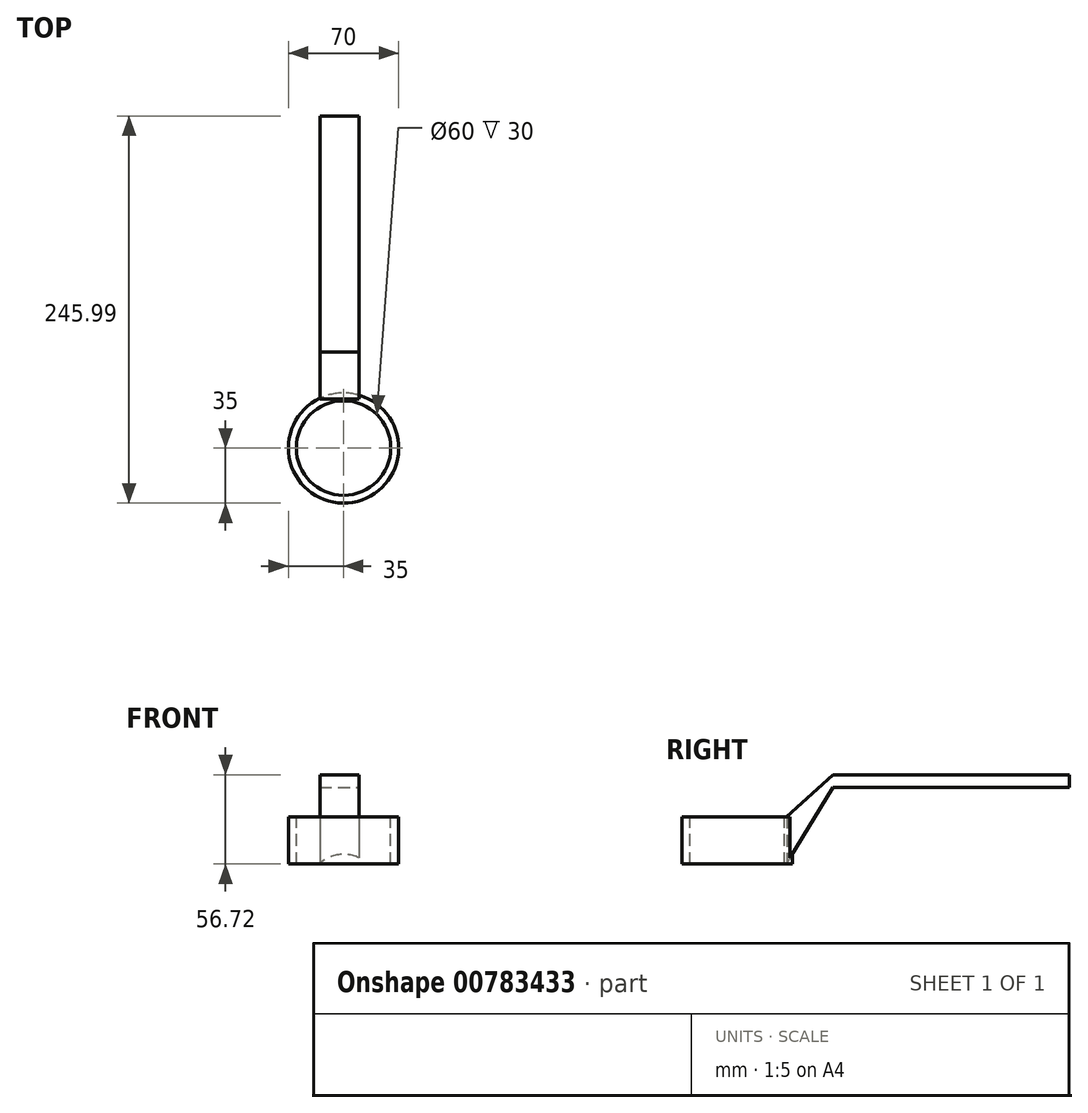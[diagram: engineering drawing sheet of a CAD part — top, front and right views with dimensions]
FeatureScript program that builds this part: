
annotation { "Feature Type Name" : "Feature", "Feature Type Description" : "" }
export const myFeature = defineFeature(function(context is Context, id is Id, definition is map)
    precondition{}
    {
        {
            var Q0;
            Q0=qCreatedBy(makeId("Top.planeOp"),FACE);
            var sketch = newSketch(context, id + "F0", { "sketchPlane" : qUnion([Q0])});
            skCircle(sketch, "E0", {"center": v(0, 0) * mm, "radius": 35 * mm});
            skSolve(sketch);
        }
        {
            var Q0;
            Q0=makeQuery(id+"F0.imprint","IMPRINT",FACE,{"disambiguationData":[TD([[makeQuery(id+"F0.imprint","IMPRINT",EDGE,{"derivedFrom":sQuery(id+"F0.wireOp",EDGE,"E0")}),1.0]])]});
            extrude(context, id + "F1", {"entities" : qUnion([Q0]), "depth" : 30 * mm, "offsetDistance" : 25.4 * mm});
        }
        {
            var Q0;
            Q0=qCreatedBy(makeId("Right.planeOp"),FACE);
            cPlane(context, id + "F2", {"entities" : qUnion([Q0]), "cplaneType" : CPlaneType.OFFSET, "offset" : 10 * mm, "width" : 152.4 * mm, "height" : 152.4 * mm});
        }
        {
            var Q0;
            Q0=qCreatedBy(id+"F2.planeOp",FACE);
            var sketch = newSketch(context, id + "F3", { "sketchPlane" : qUnion([Q0])});
            skLineSegment(sketch, "E1", {"start": v(31.23, 0) * mm, "end": v(31.23, 30) * mm});
            skLineSegment(sketch, "E2", {"start": v(31.23, 30) * mm, "end": v(61, 56.72) * mm});
            skLineSegment(sketch, "E3", {"start": v(61, 56.72) * mm, "end": v(211, 56.72) * mm});
            skLineSegment(sketch, "E4", {"start": v(211, 56.72) * mm, "end": v(211, 48.72) * mm});
            skLineSegment(sketch, "E5", {"start": v(211, 48.72) * mm, "end": v(61, 48.72) * mm});
            skLineSegment(sketch, "E6", {"start": v(61, 48.72) * mm, "end": v(31.23, 0) * mm});
            skSolve(sketch);
        }
        {
            var Q0;
            Q0=makeQuery(id+"F3.imprint","IMPRINT",FACE,{"disambiguationData":[TD([[makeQuery(id+"F3.imprint","IMPRINT",EDGE,{"derivedFrom":sQuery(id+"F3.wireOp",EDGE,"E1")}),-1.0]])]});
            extrude(context, id + "F4", {"entities" : qUnion([Q0]), "operationType" : NewBodyOperationType.ADD, "oppositeDirection" : true, "depth" : 25 * mm, "offsetDistance" : 25.4 * mm});
        }
        {
            var Q0;
            Q0=makeQuery(id+"F1.opExtrude","CAP_FACE",FACE,{"disambiguationData":[OSD([sQuery(id+"F0.wireOp",EDGE,"E0")])],"isStart":false});
            var sketch = newSketch(context, id + "F5", { "sketchPlane" : qUnion([Q0])});
            skCircle(sketch, "E7", {"center": v(0, 0) * mm, "radius": 30 * mm});
            skSolve(sketch);
        }
        {
            var Q0;
            Q0=sQuery(id+"F5.wireOp",VERTEX,"E7.center");
            var Q1;
            Q1=makeQuery(id+"F1.opExtrude","SWEPT_BODY",BODY,{"disambiguationData":[OSD([sQuery(id+"F0.wireOp",EDGE,"E0")])]});
            hole(context, id + "F6", {"style" : HoleStyle.SIMPLE, "endStyle" : HoleEndStyle.THROUGH, "holeDiameter" : 60 * mm, "majorDiameter" : 6.35 * mm, "isTappedThrough" : true, "tappedDepth" : 12.7 * mm, "tapClearance" : 3, "locations" : qUnion([Q0]), "scope" : qUnion([Q1])});
        }
    });
